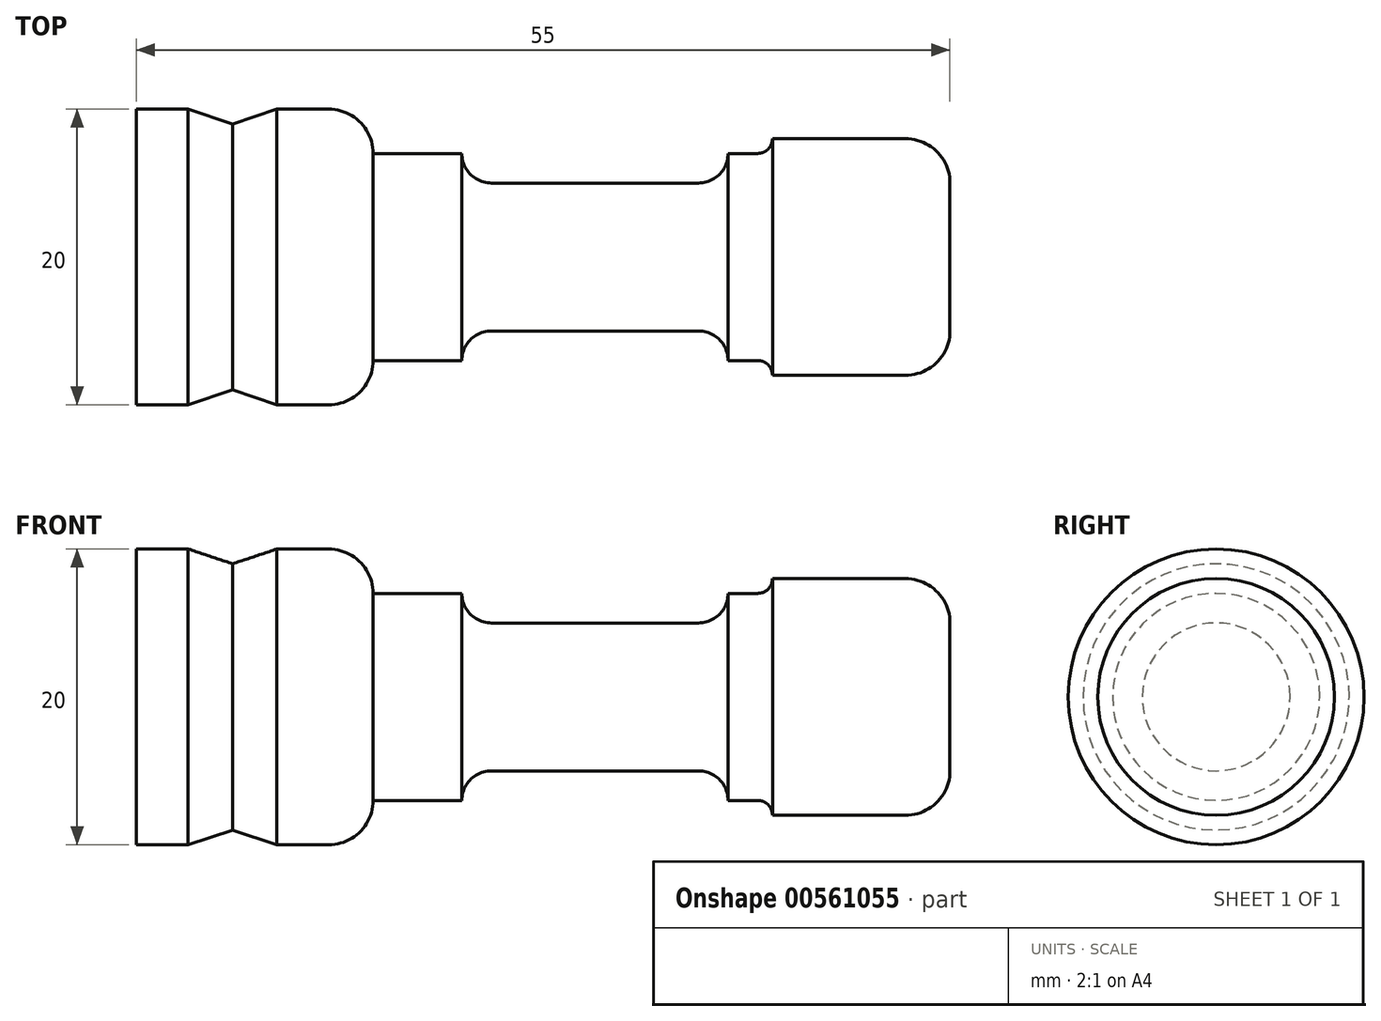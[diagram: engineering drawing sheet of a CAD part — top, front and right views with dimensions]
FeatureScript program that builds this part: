
annotation { "Feature Type Name" : "Feature", "Feature Type Description" : "" }
export const myFeature = defineFeature(function(context is Context, id is Id, definition is map)
    precondition{}
    {
        {
            var Q0;
            Q0=qCreatedBy(makeId("Front.planeOp"),FACE);
            var sketch = newSketch(context, id + "F0", { "sketchPlane" : qUnion([Q0])});
            skLineSegment(sketch, "E0", {"start": v(-30.4, 0) * mm, "end": v(24.6, 0) * mm});
            skLineSegment(sketch, "E1", {"start": v(24.6, 0) * mm, "end": v(24.6, -5) * mm});
            skLineSegment(sketch, "E2", {"start": v(21.6, -8) * mm, "end": v(12.6, -8) * mm});
            skLineSegment(sketch, "E3", {"start": v(12.6, -8) * mm, "end": v(12.6, -8) * mm});
            skLineSegment(sketch, "E4", {"start": v(11.6, -7) * mm, "end": v(9.6, -7) * mm});
            skLineSegment(sketch, "E5", {"start": v(9.6, -7) * mm, "end": v(9.6, -7) * mm});
            skLineSegment(sketch, "E6", {"start": v(7.6, -5) * mm, "end": v(-6.4, -5) * mm});
            skLineSegment(sketch, "E7", {"start": v(-8.4, -7) * mm, "end": v(-8.4, -7) * mm});
            skLineSegment(sketch, "E8", {"start": v(-8.4, -7) * mm, "end": v(-14.4, -7) * mm});
            skLineSegment(sketch, "E9", {"start": v(-14.4, -7) * mm, "end": v(-14.4, -7) * mm});
            skLineSegment(sketch, "E10", {"start": v(-17.4, -10) * mm, "end": v(-20.9, -10) * mm});
            skLineSegment(sketch, "E11", {"start": v(-26.9, -10) * mm, "end": v(-30.4, -10) * mm});
            skLineSegment(sketch, "E12", {"start": v(-30.4, -10) * mm, "end": v(-30.4, 0) * mm});
            skLineSegment(sketch, "E13", {"start": v(-23.9, -9) * mm, "end": v(-26.9, -10) * mm});
            skLineSegment(sketch, "E14", {"start": v(-23.9, -9) * mm, "end": v(-20.9, -10) * mm});
            skPoint(sketch, "E15.visualSharp", {"position": v(-8.4, -5) * mm});
            skArc(sketch, "E15.filletArc", {"start": v(-6.4, -5) * mm, "mid": v(-7.82, -5.59) * mm, "end": v(-8.4, -7) * mm});
            skPoint(sketch, "E16.visualSharp", {"position": v(-14.4, -10) * mm});
            skArc(sketch, "E16.filletArc", {"start": v(-17.4, -10) * mm, "mid": v(-15.29, -9.12) * mm, "end": v(-14.4, -7) * mm});
            skPoint(sketch, "E17.visualSharp", {"position": v(9.6, -5) * mm});
            skArc(sketch, "E17.filletArc", {"start": v(9.6, -7) * mm, "mid": v(9, -5.59) * mm, "end": v(7.6, -5) * mm});
            skPoint(sketch, "E18.visualSharp", {"position": v(12.6, -7) * mm});
            skArc(sketch, "E18.filletArc", {"start": v(12.6, -8) * mm, "mid": v(12.3, -7.3) * mm, "end": v(11.6, -7) * mm});
            skPoint(sketch, "E19.visualSharp", {"position": v(24.6, -8) * mm});
            skArc(sketch, "E19.filletArc", {"start": v(21.6, -8) * mm, "mid": v(23.71, -7.12) * mm, "end": v(24.6, -5) * mm});
            skLineSegment(sketch, "E20", {"start": v(-45.46, 0) * mm, "end": v(32.45, 0) * mm});
            skSolve(sketch);
        }
        {
            var Q0;
            Q0 = qSketchRegion(id + "F0", true);
            var Q1;
            Q1=sQuery(id+"F0.wireOp",EDGE,"E20");
            revolve(context, id + "F1", {"entities" : qUnion([Q0]), "axis" : qUnion([Q1]), "revolveType" : RevolveType.FULL});
        }
    });
